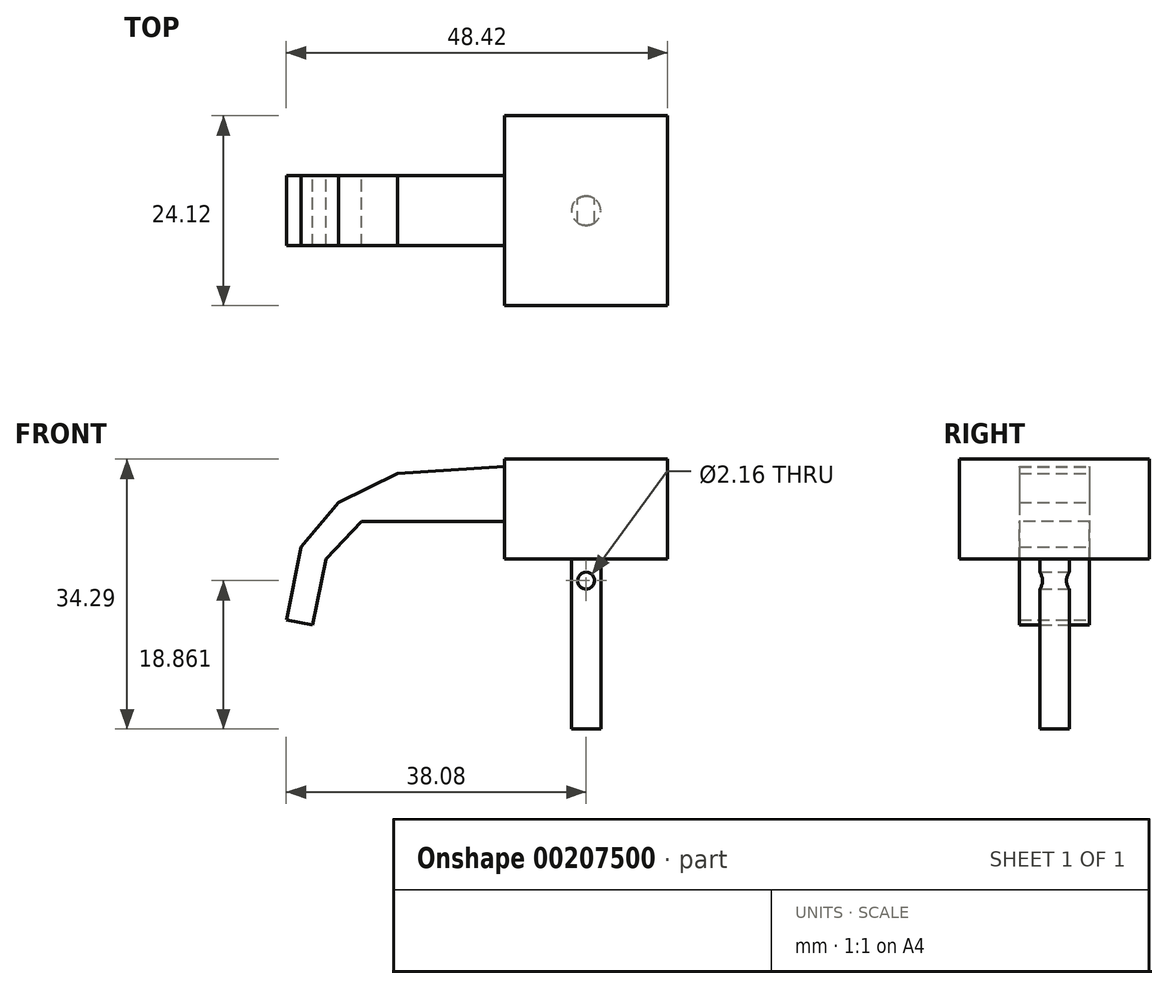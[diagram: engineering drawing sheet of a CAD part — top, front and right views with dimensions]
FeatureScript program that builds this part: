
annotation { "Feature Type Name" : "Feature", "Feature Type Description" : "" }
export const myFeature = defineFeature(function(context is Context, id is Id, definition is map)
    precondition{}
    {
        {
            var Q0;
            Q0=qCreatedBy(makeId("Top.planeOp"),FACE);
            var sketch = newSketch(context, id + "F0", { "sketchPlane" : qUnion([Q0])});
            skCircle(sketch, "E0", {"center": v(0, 0) * mm, "radius": 1.86 * mm});
            skSolve(sketch);
        }
        {
            var Q0;
            Q0 = qSketchRegion(id + "F0", true);
            extrude(context, id + "F1", {"entities" : qUnion([Q0]), "oppositeDirection" : true, "depth" : 21.59 * mm});
        }
        {
            var Q0;
            Q0=qCreatedBy(makeId("Front.planeOp"),FACE);
            var sketch = newSketch(context, id + "F2", { "sketchPlane" : qUnion([Q0])});
            skCircle(sketch, "E1", {"center": v(0, -2.73) * mm, "radius": 1.08 * mm});
            skSolve(sketch);
        }
        {
            var Q0;
            Q0 = qSketchRegion(id + "F2", true);
            extrude(context, id + "F3", {"entities" : qUnion([Q0]), "operationType" : NewBodyOperationType.REMOVE, "endBound" : BoundingType.SYMMETRIC, "depth" : 6.35 * mm});
        }
        {
            var Q0;
            Q0=qCreatedBy(makeId("Top.planeOp"),FACE);
            var sketch = newSketch(context, id + "F4", { "sketchPlane" : qUnion([Q0])});
            skLineSegment(sketch, "E2.bottom", {"start": v(10.34, 12.07) * mm, "end": v(-10.34, 12.07) * mm});
            skLineSegment(sketch, "E2.top", {"start": v(10.34, -12.07) * mm, "end": v(-10.34, -12.07) * mm});
            skLineSegment(sketch, "E2.left", {"start": v(10.34, 12.07) * mm, "end": v(10.34, -12.07) * mm});
            skLineSegment(sketch, "E2.right", {"start": v(-10.34, 12.07) * mm, "end": v(-10.34, -12.07) * mm});
            skPoint(sketch, "E2.middle", {"position": v(0, 0) * mm});
            skSolve(sketch);
        }
        {
            var Q0;
            Q0 = qSketchRegion(id + "F4", true);
            var Q1;
            Q1 = qSketchRegion(id + "F6", true);
            extrude(context, id + "F5", {"entities" : qUnion([Q0, Q1]), "operationType" : NewBodyOperationType.ADD, "depth" : 12.7 * mm});
        }
        {
            var Q0;
            Q0=qCreatedBy(makeId("Front.planeOp"),FACE);
            var sketch = newSketch(context, id + "F6", { "sketchPlane" : qUnion([Q0])});
            skLineSegment(sketch, "E3", {"start": v(-10.35, 11.78) * mm, "end": v(-23.96, 10.88) * mm});
            skLineSegment(sketch, "E4", {"start": v(-23.96, 10.88) * mm, "end": v(-31.42, 7.2) * mm});
            skLineSegment(sketch, "E5", {"start": v(-31.42, 7.2) * mm, "end": v(-36.19, 1.54) * mm});
            skLineSegment(sketch, "E6", {"start": v(-36.19, 1.54) * mm, "end": v(-38.08, -7.7) * mm});
            skLineSegment(sketch, "E7", {"start": v(-38.08, -7.7) * mm, "end": v(-34.77, -8.38) * mm});
            skLineSegment(sketch, "E8", {"start": v(-34.77, -8.38) * mm, "end": v(-33.06, 0) * mm});
            skLineSegment(sketch, "E9", {"start": v(-33.06, 0) * mm, "end": v(-28.53, 4.82) * mm});
            skLineSegment(sketch, "E10", {"start": v(-28.53, 4.82) * mm, "end": v(-21.78, 4.82) * mm});
            skLineSegment(sketch, "E11", {"start": v(-21.78, 4.82) * mm, "end": v(-9.85, 4.82) * mm});
            skLineSegment(sketch, "E12", {"start": v(-9.85, 4.82) * mm, "end": v(-10.35, 11.78) * mm});
            skSolve(sketch);
        }
        {
            var Q0;
            Q0 = qSketchRegion(id + "F6", true);
            extrude(context, id + "F7", {"entities" : qUnion([Q0]), "operationType" : NewBodyOperationType.ADD, "endBound" : BoundingType.SYMMETRIC, "depth" : 8.9 * mm});
        }
    });
